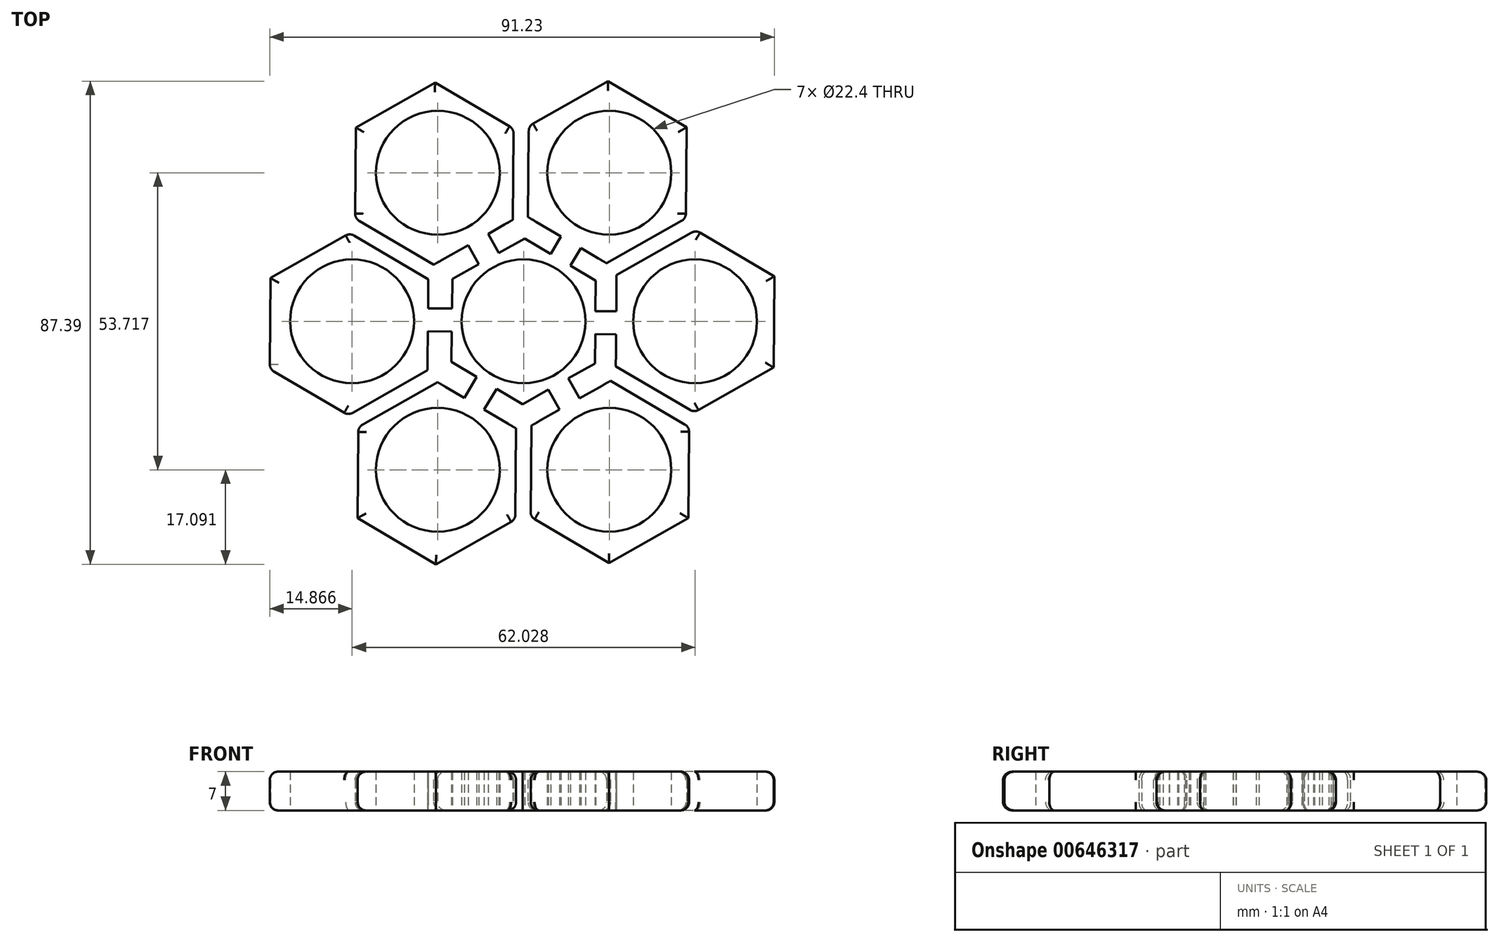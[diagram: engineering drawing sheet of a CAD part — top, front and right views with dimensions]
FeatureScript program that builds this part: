
annotation { "Feature Type Name" : "Feature", "Feature Type Description" : "" }
export const myFeature = defineFeature(function(context is Context, id is Id, definition is map)
    precondition{}
    {
        {
            var Q0;
            Q0=qCreatedBy(makeId("Top.planeOp"),FACE);
            var sketch = newSketch(context, id + "F0", { "sketchPlane" : qUnion([Q0])});
            skCircle(sketch, "E0", {"center": v(0, 0) * mm, "radius": 11.2 * mm});
            skLineSegment(sketch, "E1.0", {"start": v(12.88, -7.65) * mm, "end": v(-0.18, -14.98) * mm});
            skLineSegment(sketch, "E1.1", {"start": v(-0.18, -14.98) * mm, "end": v(-13.06, -7.33) * mm});
            skLineSegment(sketch, "E1.2", {"start": v(-13.06, -7.33) * mm, "end": v(-12.88, 7.65) * mm});
            skLineSegment(sketch, "E1.3", {"start": v(-12.88, 7.65) * mm, "end": v(0.18, 14.98) * mm});
            skLineSegment(sketch, "E1.4", {"start": v(0.18, 14.98) * mm, "end": v(13.06, 7.33) * mm});
            skLineSegment(sketch, "E1.5", {"start": v(13.06, 7.33) * mm, "end": v(12.88, -7.65) * mm});
            skPoint(sketch, "E1.0.midPoint", {"position": v(6.35, -11.31) * mm});
            skLineSegment(sketch, "E2", {"start": v(13, 1.85) * mm, "end": v(17.44, 1.8) * mm});
            skLineSegment(sketch, "E3", {"start": v(12.95, -2.3) * mm, "end": v(17.43, -2.36) * mm});
            skLineSegment(sketch, "E4.1.0", {"start": v(4.9, 12.18) * mm, "end": v(7.16, 16) * mm});
            skLineSegment(sketch, "E4.1.1", {"start": v(8.47, 10.06) * mm, "end": v(10.76, 13.91) * mm});
            skLineSegment(sketch, "E4.2.0", {"start": v(-8.1, 10.33) * mm, "end": v(-10.27, 14.2) * mm});
            skLineSegment(sketch, "E4.2.1", {"start": v(-4.48, 12.37) * mm, "end": v(-6.67, 16.28) * mm});
            skLineSegment(sketch, "E4.3.0", {"start": v(-13, -1.85) * mm, "end": v(-17.44, -1.8) * mm});
            skLineSegment(sketch, "E4.3.1", {"start": v(-12.95, 2.3) * mm, "end": v(-17.43, 2.36) * mm});
            skLineSegment(sketch, "E4.4.0", {"start": v(-4.9, -12.18) * mm, "end": v(-7.16, -16) * mm});
            skLineSegment(sketch, "E4.4.1", {"start": v(-8.47, -10.06) * mm, "end": v(-10.76, -13.91) * mm});
            skLineSegment(sketch, "E4.5.0", {"start": v(8.1, -10.33) * mm, "end": v(10.27, -14.2) * mm});
            skLineSegment(sketch, "E4.5.1", {"start": v(4.48, -12.37) * mm, "end": v(6.67, -16.28) * mm});
            skCircle(sketch, "E5", {"center": v(31.01, 0) * mm, "radius": 11.2 * mm});
            skCircle(sketch, "E6.1.0", {"center": v(15.5, 26.86) * mm, "radius": 11.2 * mm});
            skCircle(sketch, "E6.2.0", {"center": v(-15.5, 26.86) * mm, "radius": 11.2 * mm});
            skCircle(sketch, "E6.3.0", {"center": v(-31.01, 0) * mm, "radius": 11.2 * mm});
            skCircle(sketch, "E6.4.0", {"center": v(-15.5, -26.86) * mm, "radius": 11.2 * mm});
            skCircle(sketch, "E6.5.0", {"center": v(15.5, -26.86) * mm, "radius": 11.2 * mm});
            skArc(sketch, "E7.cCircle", {"start": v(16.86, 1.8) * mm, "mid": v(16.75, -0.28) * mm, "end": v(16.95, -2.36) * mm, "construction": true});
            skLineSegment(sketch, "E7.0", {"start": v(45.2, -8.35) * mm, "end": v(30.88, -16.47) * mm});
            skLineSegment(sketch, "E7.1", {"start": v(30.88, -16.47) * mm, "end": v(16.68, -8.12) * mm});
            skLineSegment(sketch, "E7.2", {"start": v(16.68, -8.12) * mm, "end": v(16.82, 8.35) * mm});
            skLineSegment(sketch, "E7.3", {"start": v(16.82, 8.35) * mm, "end": v(31.15, 16.47) * mm});
            skLineSegment(sketch, "E7.4", {"start": v(31.15, 16.47) * mm, "end": v(45.35, 8.12) * mm});
            skLineSegment(sketch, "E7.5", {"start": v(45.35, 8.12) * mm, "end": v(45.2, -8.35) * mm});
            skPoint(sketch, "E7.0.midPoint", {"position": v(38.04, -12.41) * mm});
            skLineSegment(sketch, "E8.1.0", {"start": v(0.95, 35.32) * mm, "end": v(15.28, 43.44) * mm});
            skLineSegment(sketch, "E8.1.1", {"start": v(0.81, 18.85) * mm, "end": v(0.95, 35.32) * mm});
            skLineSegment(sketch, "E8.1.2", {"start": v(15.28, 43.44) * mm, "end": v(29.48, 35.08) * mm});
            skLineSegment(sketch, "E8.1.3", {"start": v(29.48, 35.08) * mm, "end": v(29.34, 18.61) * mm});
            skLineSegment(sketch, "E8.1.4", {"start": v(29.34, 18.61) * mm, "end": v(15.01, 10.5) * mm});
            skLineSegment(sketch, "E8.1.5", {"start": v(15.01, 10.5) * mm, "end": v(0.81, 18.85) * mm});
            skLineSegment(sketch, "E8.2.0", {"start": v(-30.47, 18.59) * mm, "end": v(-30.34, 35.06) * mm});
            skLineSegment(sketch, "E8.2.1", {"start": v(-16.28, 10.24) * mm, "end": v(-30.47, 18.59) * mm});
            skLineSegment(sketch, "E8.2.2", {"start": v(-30.34, 35.06) * mm, "end": v(-16, 43.18) * mm});
            skLineSegment(sketch, "E8.2.3", {"start": v(-16, 43.18) * mm, "end": v(-1.8, 34.82) * mm});
            skLineSegment(sketch, "E8.2.4", {"start": v(-1.8, 34.82) * mm, "end": v(-1.95, 18.35) * mm});
            skLineSegment(sketch, "E8.2.5", {"start": v(-1.95, 18.35) * mm, "end": v(-16.28, 10.24) * mm});
            skPoint(sketch, "E8.center", {"position": v(-0.27, -0.26) * mm});
            skLineSegment(sketch, "E9.1.3.0", {"start": v(-31.7, -16.99) * mm, "end": v(-45.9, -8.64) * mm});
            skLineSegment(sketch, "E9.3.3.0", {"start": v(-17.36, -8.87) * mm, "end": v(-31.7, -16.99) * mm});
            skLineSegment(sketch, "E9.6.3.0", {"start": v(-45.9, -8.64) * mm, "end": v(-45.76, 7.83) * mm});
            skLineSegment(sketch, "E9.9.3.0", {"start": v(-45.76, 7.83) * mm, "end": v(-31.42, 15.95) * mm});
            skLineSegment(sketch, "E9.12.3.0", {"start": v(-31.42, 15.95) * mm, "end": v(-17.23, 7.6) * mm});
            skLineSegment(sketch, "E9.15.3.0", {"start": v(-17.23, 7.6) * mm, "end": v(-17.36, -8.87) * mm});
            skLineSegment(sketch, "E9.1.4.0", {"start": v(-1.5, -35.84) * mm, "end": v(-15.83, -43.95) * mm});
            skLineSegment(sketch, "E9.3.4.0", {"start": v(-1.36, -19.37) * mm, "end": v(-1.5, -35.84) * mm});
            skLineSegment(sketch, "E9.6.4.0", {"start": v(-15.83, -43.95) * mm, "end": v(-30.02, -35.6) * mm});
            skLineSegment(sketch, "E9.9.4.0", {"start": v(-30.02, -35.6) * mm, "end": v(-29.89, -19.13) * mm});
            skLineSegment(sketch, "E9.12.4.0", {"start": v(-29.89, -19.13) * mm, "end": v(-15.56, -11.01) * mm});
            skLineSegment(sketch, "E9.15.4.0", {"start": v(-15.56, -11.01) * mm, "end": v(-1.36, -19.37) * mm});
            skLineSegment(sketch, "E9.1.5.0", {"start": v(29.93, -19.1) * mm, "end": v(29.8, -35.58) * mm});
            skLineSegment(sketch, "E9.3.5.0", {"start": v(15.73, -10.75) * mm, "end": v(29.93, -19.1) * mm});
            skLineSegment(sketch, "E9.6.5.0", {"start": v(29.8, -35.58) * mm, "end": v(15.46, -43.7) * mm});
            skLineSegment(sketch, "E9.9.5.0", {"start": v(15.46, -43.7) * mm, "end": v(1.26, -35.34) * mm});
            skLineSegment(sketch, "E9.12.5.0", {"start": v(1.26, -35.34) * mm, "end": v(1.4, -18.87) * mm});
            skLineSegment(sketch, "E9.15.5.0", {"start": v(1.4, -18.87) * mm, "end": v(15.73, -10.75) * mm});
            skLineSegment(sketch, "E10", {"start": v(-25.72, 12.6) * mm, "end": v(-26.2, 11.78) * mm});
            skPoint(sketch, "E10.startSnap0", {"position": v(-24.33, 11.78) * mm});
            skPoint(sketch, "E10.endSnap0", {"position": v(-24.33, 11.78) * mm});
            skLineSegment(sketch, "E11.1.0", {"start": v(-21.1, -14.15) * mm, "end": v(-20.97, -14.4) * mm});
            skLineSegment(sketch, "E11.1.1", {"start": v(-23.9, -15.74) * mm, "end": v(-23.3, -16.8) * mm});
            skLineSegment(sketch, "E11.2.0", {"start": v(1.35, -25.35) * mm, "end": v(1.98, -25.36) * mm});
            skLineSegment(sketch, "E11.2.1", {"start": v(1.32, -28.57) * mm, "end": v(2.9, -28.59) * mm});
            skLineSegment(sketch, "E11.3.0", {"start": v(22.58, -11.59) * mm, "end": v(22.95, -10.96) * mm});
            skLineSegment(sketch, "E11.3.1", {"start": v(25.36, -13.22) * mm, "end": v(26.2, -11.78) * mm});
            skLineSegment(sketch, "E11.4.0", {"start": v(21.2, 14) * mm, "end": v(20.97, 14.4) * mm});
            skLineSegment(sketch, "E11.4.1", {"start": v(24, 15.59) * mm, "end": v(23.3, 16.8) * mm});
            skLineSegment(sketch, "E11.5.0", {"start": v(-1.89, 25.35) * mm, "end": v(-1.98, 25.36) * mm});
            skLineSegment(sketch, "E11.5.1", {"start": v(-1.86, 28.58) * mm, "end": v(-2.9, 28.59) * mm});
            skPoint(sketch, "E12.orphan", {"position": v(-24.33, 14.97) * mm});
            skPoint(sketch, "E13.orphan", {"position": v(0.78, 25.33) * mm});
            skPoint(sketch, "E14.orphan", {"position": v(0.8, 28.55) * mm});
            skPoint(sketch, "E15.orphan", {"position": v(25.13, 13.58) * mm});
            skPoint(sketch, "E16.orphan", {"position": v(22.33, 12) * mm});
            skPoint(sketch, "E17.orphan", {"position": v(21.55, -13.34) * mm});
            skPoint(sketch, "E18.orphan", {"position": v(24.33, -14.97) * mm});
            skPoint(sketch, "E19.orphan", {"position": v(-0.8, -28.55) * mm});
            skPoint(sketch, "E20.orphan", {"position": v(-0.78, -25.33) * mm});
            skPoint(sketch, "E21.orphan", {"position": v(-25.13, -13.58) * mm});
            skPoint(sketch, "E22.orphan", {"position": v(-22.33, -12) * mm});
            skSolve(sketch);
        }
        {
            var Q0;
            Q0=makeQuery(id+"F0.imprint","IMPRINT",FACE,{"disambiguationData":[TD([[makeQuery(id+"F0.imprint","IMPRINT",EDGE,{"derivedFrom":sQuery(id+"F0.wireOp",EDGE,"E6.3.0")}),-1.0]])]});
            var Q1;
            Q1=makeQuery(id+"F0.imprint","IMPRINT",FACE,{"disambiguationData":[TD([[makeQuery(id+"F0.imprint","IMPRINT",EDGE,{"derivedFrom":sQuery(id+"F0.wireOp",EDGE,"E0")}),-1.0]])]});
            var Q2;
            Q2=makeQuery(id+"F0.imprint","IMPRINT",FACE,{"disambiguationData":[TD([[makeQuery(id+"F0.imprint","IMPRINT",EDGE,{"derivedFrom":sQuery(id+"F0.wireOp",EDGE,"E6.2.0")}),-1.0]])]});
            var Q3;
            Q3=makeQuery(id+"F0.imprint","IMPRINT",FACE,{"disambiguationData":[TD([[makeQuery(id+"F0.imprint","IMPRINT",EDGE,{"derivedFrom":sQuery(id+"F0.wireOp",EDGE,"E6.1.0")}),-1.0]])]});
            var Q4;
            Q4=makeQuery(id+"F0.imprint","IMPRINT",FACE,{"disambiguationData":[TD([[makeQuery(id+"F0.imprint","IMPRINT",EDGE,{"derivedFrom":sQuery(id+"F0.wireOp",EDGE,"E5")}),-1.0]])]});
            var Q5;
            Q5=makeQuery(id+"F0.imprint","IMPRINT",FACE,{"disambiguationData":[TD([[makeQuery(id+"F0.imprint","IMPRINT",EDGE,{"derivedFrom":sQuery(id+"F0.wireOp",EDGE,"E6.5.0")}),-1.0]])]});
            var Q6;
            Q6=makeQuery(id+"F0.imprint","IMPRINT",FACE,{"disambiguationData":[TD([[makeQuery(id+"F0.imprint","IMPRINT",EDGE,{"derivedFrom":sQuery(id+"F0.wireOp",EDGE,"E6.4.0")}),-1.0]])]});
            var Q7;
            {var subQ0=sQuery(id+"F0.wireOp",EDGE,"E4.4.0");var subQ1=sQuery(id+"F0.wireOp",EDGE,"E1.1");var subQ2=makeQuery(id+"F0.imprint","INTERSECT",VERTEX,{"derivedFrom":[subQ1,subQ0]});Q7=makeQuery(id+"F0.imprint","IMPRINT",FACE,{"disambiguationData":[TD([[makeQuery(id+"F0.imprint","IMPRINT",EDGE,{"disambiguationData":[TD([[subQ2,-1.0]])],"derivedFrom":subQ1}),1.0]])]});}
            var Q8;
            {var subQ0=sQuery(id+"F0.wireOp",EDGE,"E4.5.0");var subQ1=sQuery(id+"F0.wireOp",EDGE,"E1.0");var subQ2=makeQuery(id+"F0.imprint","INTERSECT",VERTEX,{"derivedFrom":[subQ1,subQ0]});Q8=makeQuery(id+"F0.imprint","IMPRINT",FACE,{"disambiguationData":[TD([[makeQuery(id+"F0.imprint","IMPRINT",EDGE,{"disambiguationData":[TD([[subQ2,-1.0]])],"derivedFrom":subQ1}),1.0]])]});}
            var Q9;
            {var subQ0=sQuery(id+"F0.wireOp",EDGE,"E2");var subQ1=sQuery(id+"F0.wireOp",EDGE,"E1.5");var subQ2=makeQuery(id+"F0.imprint","INTERSECT",VERTEX,{"derivedFrom":[subQ1,subQ0]});Q9=makeQuery(id+"F0.imprint","IMPRINT",FACE,{"disambiguationData":[TD([[makeQuery(id+"F0.imprint","IMPRINT",EDGE,{"disambiguationData":[TD([[subQ2,-1.0]])],"derivedFrom":subQ1}),1.0]])]});}
            var Q10;
            {var subQ0=sQuery(id+"F0.wireOp",EDGE,"E4.1.0");var subQ1=sQuery(id+"F0.wireOp",EDGE,"E1.4");var subQ2=makeQuery(id+"F0.imprint","INTERSECT",VERTEX,{"derivedFrom":[subQ1,subQ0]});Q10=makeQuery(id+"F0.imprint","IMPRINT",FACE,{"disambiguationData":[TD([[makeQuery(id+"F0.imprint","IMPRINT",EDGE,{"disambiguationData":[TD([[subQ2,-1.0]])],"derivedFrom":subQ1}),1.0]])]});}
            var Q11;
            {var subQ0=sQuery(id+"F0.wireOp",EDGE,"E4.2.0");var subQ1=sQuery(id+"F0.wireOp",EDGE,"E1.3");var subQ2=makeQuery(id+"F0.imprint","INTERSECT",VERTEX,{"derivedFrom":[subQ1,subQ0]});Q11=makeQuery(id+"F0.imprint","IMPRINT",FACE,{"disambiguationData":[TD([[makeQuery(id+"F0.imprint","IMPRINT",EDGE,{"disambiguationData":[TD([[subQ2,-1.0]])],"derivedFrom":subQ1}),1.0]])]});}
            var Q12;
            {var subQ0=sQuery(id+"F0.wireOp",EDGE,"E4.3.0");var subQ1=sQuery(id+"F0.wireOp",EDGE,"E1.2");var subQ2=makeQuery(id+"F0.imprint","INTERSECT",VERTEX,{"derivedFrom":[subQ1,subQ0]});Q12=makeQuery(id+"F0.imprint","IMPRINT",FACE,{"disambiguationData":[TD([[makeQuery(id+"F0.imprint","IMPRINT",EDGE,{"disambiguationData":[TD([[subQ2,-1.0]])],"derivedFrom":subQ1}),1.0]])]});}
            extrude(context, id + "F1", {"entities" : qUnion([Q0, Q1, Q2, Q3, Q4, Q5, Q6, Q7, Q8, Q9, Q10, Q11, Q12]), "depth" : 7 * mm, "offsetDistance" : 25 * mm});
        }
        {
            var Q0;
            Q0=makeQuery(id+"F1.opExtrude","CAP_EDGE",EDGE,{"disambiguationData":[OSD([sQuery(id+"F0.wireOp",EDGE,"E9.6.5.0")])],"isStart":false});
            var Q1;
            Q1=makeQuery(id+"F1.opExtrude","CAP_EDGE",EDGE,{"disambiguationData":[OSD([sQuery(id+"F0.wireOp",EDGE,"E9.9.5.0")])],"isStart":false});
            var Q2;
            Q2=makeQuery(id+"F1.opExtrude","CAP_EDGE",EDGE,{"disambiguationData":[OSD([sQuery(id+"F0.wireOp",EDGE,"E9.1.4.0")])],"isStart":false});
            var Q3;
            Q3=makeQuery(id+"F1.opExtrude","CAP_EDGE",EDGE,{"disambiguationData":[OSD([sQuery(id+"F0.wireOp",EDGE,"E9.6.4.0")])],"isStart":false});
            var Q4;
            Q4=makeQuery(id+"F1.opExtrude","CAP_EDGE",EDGE,{"disambiguationData":[OSD([sQuery(id+"F0.wireOp",EDGE,"E9.9.4.0")])],"isStart":false});
            var Q5;
            Q5=makeQuery(id+"F1.opExtrude","CAP_EDGE",EDGE,{"disambiguationData":[OSD([sQuery(id+"F0.wireOp",EDGE,"E9.1.3.0")])],"isStart":false});
            var Q6;
            Q6=makeQuery(id+"F1.opExtrude","CAP_EDGE",EDGE,{"disambiguationData":[OSD([sQuery(id+"F0.wireOp",EDGE,"E9.6.3.0")])],"isStart":false});
            var Q7;
            Q7=makeQuery(id+"F1.opExtrude","CAP_EDGE",EDGE,{"disambiguationData":[OSD([sQuery(id+"F0.wireOp",EDGE,"E9.9.3.0")])],"isStart":false});
            var Q8;
            Q8=makeQuery(id+"F1.opExtrude","CAP_EDGE",EDGE,{"disambiguationData":[OSD([sQuery(id+"F0.wireOp",EDGE,"E8.2.0")])],"isStart":false});
            var Q9;
            Q9=makeQuery(id+"F1.opExtrude","CAP_EDGE",EDGE,{"disambiguationData":[OSD([sQuery(id+"F0.wireOp",EDGE,"E8.2.2")])],"isStart":false});
            var Q10;
            Q10=makeQuery(id+"F1.opExtrude","CAP_EDGE",EDGE,{"disambiguationData":[OSD([sQuery(id+"F0.wireOp",EDGE,"E8.2.3")])],"isStart":false});
            var Q11;
            Q11=makeQuery(id+"F1.opExtrude","CAP_EDGE",EDGE,{"disambiguationData":[OSD([sQuery(id+"F0.wireOp",EDGE,"E8.1.0")])],"isStart":false});
            var Q12;
            Q12=makeQuery(id+"F1.opExtrude","CAP_EDGE",EDGE,{"disambiguationData":[OSD([sQuery(id+"F0.wireOp",EDGE,"E8.1.2")])],"isStart":false});
            var Q13;
            Q13=makeQuery(id+"F1.opExtrude","CAP_EDGE",EDGE,{"disambiguationData":[OSD([sQuery(id+"F0.wireOp",EDGE,"E7.4")])],"isStart":false});
            var Q14;
            Q14=makeQuery(id+"F1.opExtrude","CAP_EDGE",EDGE,{"disambiguationData":[OSD([sQuery(id+"F0.wireOp",EDGE,"E8.1.3")])],"isStart":false});
            var Q15;
            Q15=makeQuery(id+"F1.opExtrude","CAP_EDGE",EDGE,{"disambiguationData":[OSD([sQuery(id+"F0.wireOp",EDGE,"E7.5")])],"isStart":false});
            var Q16;
            Q16=makeQuery(id+"F1.opExtrude","CAP_EDGE",EDGE,{"disambiguationData":[OSD([sQuery(id+"F0.wireOp",EDGE,"E7.0")])],"isStart":false});
            var Q17;
            Q17=makeQuery(id+"F1.opExtrude","CAP_EDGE",EDGE,{"disambiguationData":[OSD([sQuery(id+"F0.wireOp",EDGE,"E9.1.5.0")])],"isStart":false});
            fillet(context, id + "F2", {"entities" : qUnion([Q0, Q1, Q2, Q3, Q4, Q5, Q6, Q7, Q8, Q9, Q10, Q11, Q12, Q13, Q14, Q15, Q16, Q17]), "radius" : 1.5 * mm, "tangentPropagation" : true, "allowEdgeOverflow" : false});
        }
        {
            var Q0;
            Q0=makeQuery(id+"F1.opExtrude","CAP_EDGE",EDGE,{"disambiguationData":[OSD([sQuery(id+"F0.wireOp",EDGE,"E9.9.3.0")])],"isStart":true});
            var Q1;
            Q1=makeQuery(id+"F1.opExtrude","CAP_EDGE",EDGE,{"disambiguationData":[OSD([sQuery(id+"F0.wireOp",EDGE,"E9.6.3.0")])],"isStart":true});
            var Q2;
            Q2=makeQuery(id+"F1.opExtrude","CAP_EDGE",EDGE,{"disambiguationData":[OSD([sQuery(id+"F0.wireOp",EDGE,"E9.9.4.0")])],"isStart":true});
            var Q3;
            Q3=makeQuery(id+"F1.opExtrude","CAP_EDGE",EDGE,{"disambiguationData":[OSD([sQuery(id+"F0.wireOp",EDGE,"E9.6.4.0")])],"isStart":true});
            var Q4;
            Q4=makeQuery(id+"F1.opExtrude","CAP_EDGE",EDGE,{"disambiguationData":[OSD([sQuery(id+"F0.wireOp",EDGE,"E9.1.4.0")])],"isStart":true});
            var Q5;
            Q5=makeQuery(id+"F1.opExtrude","CAP_EDGE",EDGE,{"disambiguationData":[OSD([sQuery(id+"F0.wireOp",EDGE,"E9.9.5.0")])],"isStart":true});
            var Q6;
            Q6=makeQuery(id+"F1.opExtrude","CAP_EDGE",EDGE,{"disambiguationData":[OSD([sQuery(id+"F0.wireOp",EDGE,"E9.6.5.0")])],"isStart":true});
            var Q7;
            Q7=makeQuery(id+"F1.opExtrude","CAP_EDGE",EDGE,{"disambiguationData":[OSD([sQuery(id+"F0.wireOp",EDGE,"E9.1.5.0")])],"isStart":true});
            var Q8;
            Q8=makeQuery(id+"F1.opExtrude","CAP_EDGE",EDGE,{"disambiguationData":[OSD([sQuery(id+"F0.wireOp",EDGE,"E7.0")])],"isStart":true});
            var Q9;
            Q9=makeQuery(id+"F1.opExtrude","CAP_EDGE",EDGE,{"disambiguationData":[OSD([sQuery(id+"F0.wireOp",EDGE,"E7.5")])],"isStart":true});
            var Q10;
            Q10=makeQuery(id+"F1.opExtrude","CAP_EDGE",EDGE,{"disambiguationData":[OSD([sQuery(id+"F0.wireOp",EDGE,"E8.1.2")])],"isStart":true});
            var Q11;
            Q11=makeQuery(id+"F1.opExtrude","CAP_EDGE",EDGE,{"disambiguationData":[OSD([sQuery(id+"F0.wireOp",EDGE,"E7.4")])],"isStart":true});
            var Q12;
            Q12=makeQuery(id+"F1.opExtrude","CAP_EDGE",EDGE,{"disambiguationData":[OSD([sQuery(id+"F0.wireOp",EDGE,"E8.1.3")])],"isStart":true});
            var Q13;
            Q13=makeQuery(id+"F1.opExtrude","CAP_EDGE",EDGE,{"disambiguationData":[OSD([sQuery(id+"F0.wireOp",EDGE,"E8.1.0")])],"isStart":true});
            var Q14;
            Q14=makeQuery(id+"F1.opExtrude","CAP_EDGE",EDGE,{"disambiguationData":[OSD([sQuery(id+"F0.wireOp",EDGE,"E8.2.3")])],"isStart":true});
            var Q15;
            Q15=makeQuery(id+"F1.opExtrude","CAP_EDGE",EDGE,{"disambiguationData":[OSD([sQuery(id+"F0.wireOp",EDGE,"E8.2.2")])],"isStart":true});
            var Q16;
            Q16=makeQuery(id+"F1.opExtrude","CAP_EDGE",EDGE,{"disambiguationData":[OSD([sQuery(id+"F0.wireOp",EDGE,"E8.2.0")])],"isStart":true});
            fillet(context, id + "F3", {"entities" : qUnion([Q0, Q1, Q2, Q3, Q4, Q5, Q6, Q7, Q8, Q9, Q10, Q11, Q12, Q13, Q14, Q15, Q16]), "radius" : 1.5 * mm, "tangentPropagation" : true, "allowEdgeOverflow" : false});
        }
        {
            var Q0;
            Q0=makeQuery(id+"F1.opExtrude","CAP_EDGE",EDGE,{"disambiguationData":[OSD([sQuery(id+"F0.wireOp",EDGE,"E8.2.1")])],"isStart":false});
            var Q1;
            Q1=makeQuery(id+"F1.opExtrude","CAP_EDGE",EDGE,{"disambiguationData":[OSD([sQuery(id+"F0.wireOp",EDGE,"E8.2.4")])],"isStart":false});
            var Q2;
            Q2=makeQuery(id+"F1.opExtrude","CAP_EDGE",EDGE,{"disambiguationData":[OSD([sQuery(id+"F0.wireOp",EDGE,"E8.1.1")])],"isStart":false});
            var Q3;
            Q3=makeQuery(id+"F1.opExtrude","CAP_EDGE",EDGE,{"disambiguationData":[OSD([sQuery(id+"F0.wireOp",EDGE,"E8.1.4")])],"isStart":false});
            var Q4;
            Q4=makeQuery(id+"F1.opExtrude","CAP_EDGE",EDGE,{"disambiguationData":[OSD([sQuery(id+"F0.wireOp",EDGE,"E7.3")])],"isStart":false});
            var Q5;
            Q5=makeQuery(id+"F1.opExtrude","CAP_EDGE",EDGE,{"disambiguationData":[OSD([sQuery(id+"F0.wireOp",EDGE,"E7.1")])],"isStart":false});
            var Q6;
            Q6=makeQuery(id+"F1.opExtrude","CAP_EDGE",EDGE,{"disambiguationData":[OSD([sQuery(id+"F0.wireOp",EDGE,"E9.3.5.0")])],"isStart":false});
            var Q7;
            Q7=makeQuery(id+"F1.opExtrude","CAP_EDGE",EDGE,{"disambiguationData":[OSD([sQuery(id+"F0.wireOp",EDGE,"E9.12.5.0")])],"isStart":false});
            var Q8;
            Q8=makeQuery(id+"F1.opExtrude","CAP_EDGE",EDGE,{"disambiguationData":[OSD([sQuery(id+"F0.wireOp",EDGE,"E9.3.4.0")])],"isStart":false});
            var Q9;
            Q9=makeQuery(id+"F1.opExtrude","CAP_EDGE",EDGE,{"disambiguationData":[OSD([sQuery(id+"F0.wireOp",EDGE,"E9.12.4.0")])],"isStart":false});
            var Q10;
            Q10=makeQuery(id+"F1.opExtrude","CAP_EDGE",EDGE,{"disambiguationData":[OSD([sQuery(id+"F0.wireOp",EDGE,"E9.3.3.0")])],"isStart":false});
            var Q11;
            Q11=makeQuery(id+"F1.opExtrude","CAP_EDGE",EDGE,{"disambiguationData":[OSD([sQuery(id+"F0.wireOp",EDGE,"E9.12.3.0")])],"isStart":false});
            fillet(context, id + "F4", {"entities" : qUnion([Q0, Q1, Q2, Q3, Q4, Q5, Q6, Q7, Q8, Q9, Q10, Q11]), "radius" : 1.5 * mm, "tangentPropagation" : true, "allowEdgeOverflow" : false});
        }
        {
            var Q0;
            Q0=makeQuery(id+"F1.opExtrude","CAP_EDGE",EDGE,{"disambiguationData":[OSD([sQuery(id+"F0.wireOp",EDGE,"E9.1.3.0")])],"isStart":true});
            var Q1;
            Q1=makeQuery(id+"F1.opExtrude","CAP_EDGE",EDGE,{"disambiguationData":[OSD([sQuery(id+"F0.wireOp",EDGE,"E9.3.3.0")])],"isStart":true});
            fillet(context, id + "F5", {"entities" : qUnion([Q0, Q1]), "radius" : 1.5 * mm, "tangentPropagation" : true, "allowEdgeOverflow" : false});
        }
    });
